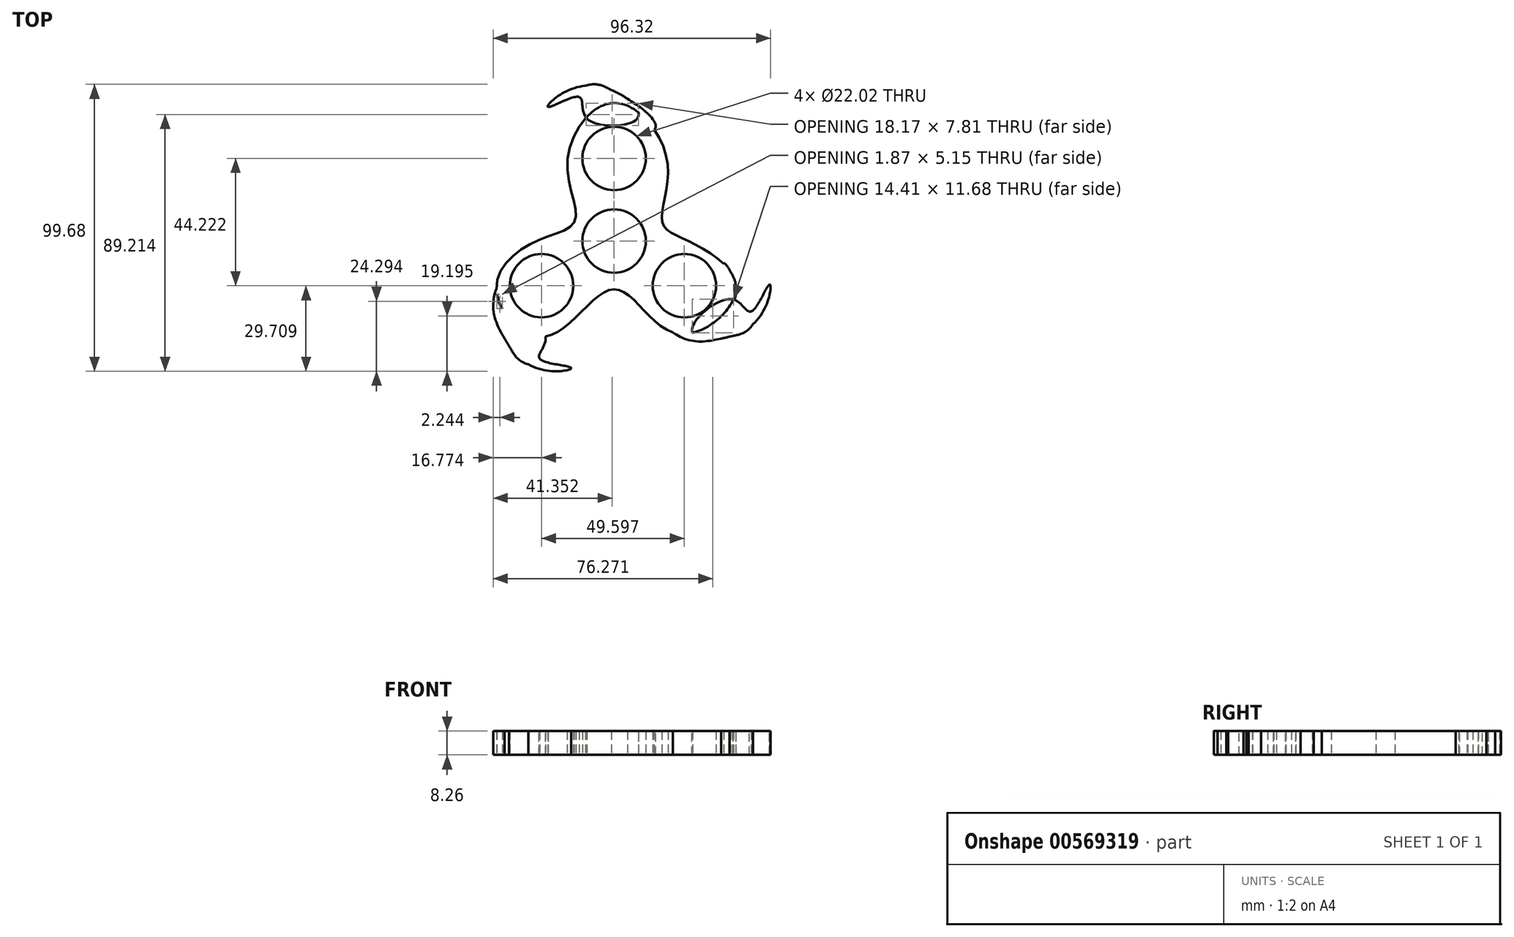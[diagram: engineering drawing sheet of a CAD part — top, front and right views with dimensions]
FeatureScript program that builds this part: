
annotation { "Feature Type Name" : "Feature", "Feature Type Description" : "" }
export const myFeature = defineFeature(function(context is Context, id is Id, definition is map)
    precondition{}
    {
        {
            var Q0;
            Q0=qCreatedBy(makeId("Top.planeOp"),FACE);
            var sketch = newSketch(context, id + "F0", { "sketchPlane" : qUnion([Q0])});
            skFitSpline(sketch, "E0", {"points": [v(0, 64.69) * mm, v(-16.17, 45.11) * mm, v(-13.62, 23.83) * mm, v(-26.95, 16.74) * mm, v(-40.86, 0) * mm, v(-23.83, -16.46) * mm, v(0, 0) * mm, v(21.56, -15.32) * mm, v(42.27, 0) * mm, v(26.39, 16.46) * mm, v(16.74, 23.27) * mm, v(18.44, 44.54) * mm, v(0, 64.69) * mm]});
            skCircle(sketch, "E1", {"center": v(0, 45.44) * mm, "radius": 11.01 * mm});
            skCircle(sketch, "E2", {"center": v(24.4, 1.22) * mm, "radius": 11.01 * mm});
            skCircle(sketch, "E3", {"center": v(0, 16.74) * mm, "radius": 11.01 * mm});
            skCircle(sketch, "E4", {"center": v(-25.2, 1.22) * mm, "radius": 11.01 * mm});
            skFitSpline(sketch, "E5", {"points": [v(-38.8, -6.77) * mm, v(-29.8, -26.1) * mm, v(-15.04, -27.24) * mm, v(-25.82, -24.12) * mm, v(-23.83, -16.46) * mm, v(-38.8, -6.77) * mm]});
            skFitSpline(sketch, "E6", {"points": [v(-36.45, -19.69) * mm, v(-41.9, -7.25) * mm, v(-40.86, 0) * mm, v(-38.8, -6.77) * mm, v(-23.83, -16.46) * mm, v(-25.82, -24.12) * mm, v(-15.04, -27.24) * mm, v(-29.8, -26.1) * mm, v(-36.45, -19.69) * mm]});
            skFitSpline(sketch, "E7", {"points": [v(27.1, -14.7) * mm, v(48.26, -12.1) * mm, v(53.9, 1.59) * mm, v(47.6, -7.7) * mm, v(40.93, -3.45) * mm, v(27.1, -14.7) * mm]});
            skFitSpline(sketch, "E8", {"points": [v(40.1, -16.46) * mm, v(26.59, -17.8) * mm, v(20.02, -14.57) * mm, v(27.1, -14.7) * mm, v(40.93, -3.45) * mm, v(47.6, -7.7) * mm, v(53.9, 1.59) * mm, v(48.26, -12.1) * mm, v(40.1, -16.46) * mm]});
            skFitSpline(sketch, "E9", {"points": [v(8.33, 59.78) * mm, v(-10, 70.67) * mm, v(-22.83, 63.28) * mm, v(-12.17, 66.79) * mm, v(-9.48, 59.34) * mm, v(8.33, 59.78) * mm]});
            skFitSpline(sketch, "E10", {"points": [v(-0.89, 69.13) * mm, v(10.63, 61.94) * mm, v(13.86, 55.36) * mm, v(-9.48, 59.34) * mm, v(-12.17, 66.79) * mm, v(-22.83, 63.28) * mm, v(-10, 70.67) * mm, v(-0.89, 69.13) * mm]});
            skFitSpline(sketch, "E11", {"points": [v(38, 8.9) * mm, v(42.27, 0) * mm, v(40.93, -3.45) * mm, v(38, 8.9) * mm]});
            skSolve(sketch);
        }
        {
            var Q0;
            Q0 = qSketchRegion(id + "F0", true);
            extrude(context, id + "F1", {"entities" : qUnion([Q0]), "depth" : 8.25 * mm, "offsetDistance" : 25.4 * mm});
        }
    });
